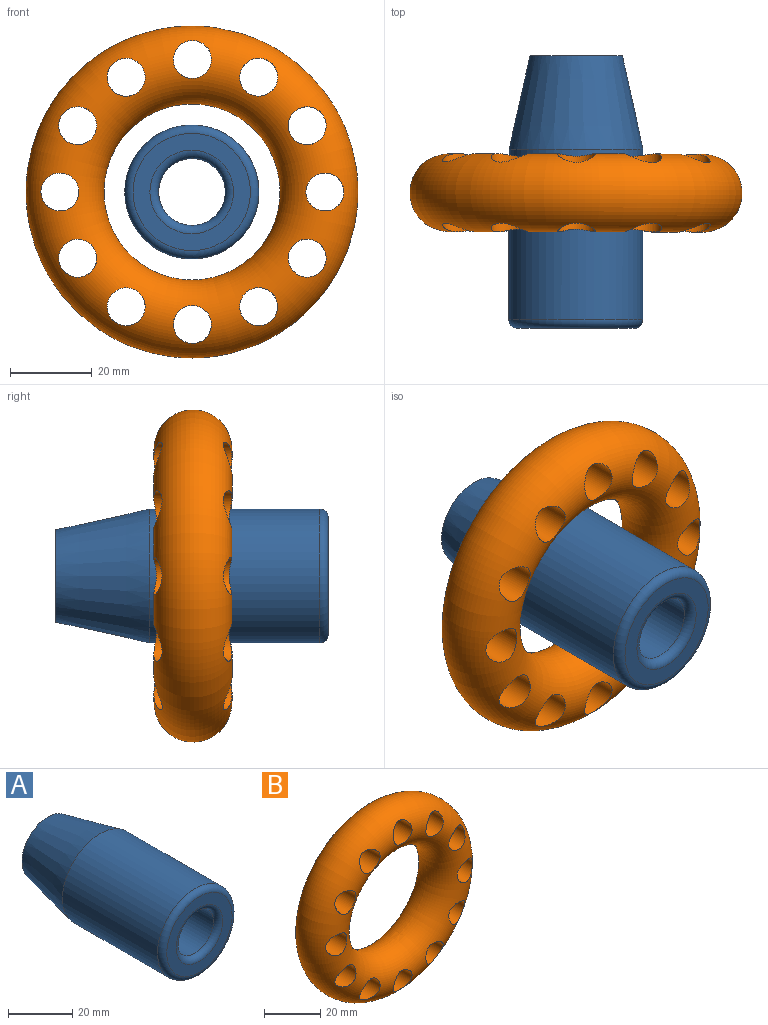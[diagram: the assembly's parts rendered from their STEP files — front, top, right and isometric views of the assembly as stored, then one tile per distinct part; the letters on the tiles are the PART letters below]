
ASSEMBLY  parts=2 mates=1
PART A: 8 faces, bbox 35.4x66.5x35.4 mm
  f0: cylinder r=16.36mm len=41.66mm, axis (0,1,0), area 4282.4mm2, adj f5,f7
  f1: plane 28.66x28.66mm, normal (0,-1,0), area 317.4mm2, adj f4,f5
  f2: plane 22.56x22.56mm, normal (0,1,0), area 38.7mm2, adj f6,f7
  f3: cylinder r=8.18mm len=61.98mm, axis (0,-1,0), area 3186mm2, adj f4,f6
  f4: torus R=10.21mm, axis (0,-1,0), area 178.9mm2, adj f1,f3
  f5: torus R=14.33mm, axis (0,-1,0), area 313.3mm2, adj f0,f1
  f6: cone r=10.72mm half-angle=45deg, axis (0,1,0), area 213.3mm2, adj f2,f3
  f7: cone r=16.36mm half-angle=12.5deg, axis (0,-1,0), area 2033.7mm2, adj f0,f2
PART B: 13 faces, bbox 87.8x19.2x87.8 mm
  f0: cylinder r=4.64mm len=19.06mm, axis (0,-1,0), area 511.6mm2, adj f11
  f1: cylinder r=4.64mm len=19.05mm, axis (0,-1,0), area 511.2mm2, adj f11
  f2: cylinder r=4.64mm len=19.04mm, axis (0,-1,0), area 511.1mm2, adj f11
  f3: cylinder r=4.64mm len=19.05mm, axis (0,-1,0), area 511.2mm2, adj f11
  f4: cylinder r=4.64mm len=19.06mm, axis (0,-1,0), area 511.6mm2, adj f11
  f5: cylinder r=4.64mm len=19.06mm, axis (0,-1,0), area 512.2mm2, adj f11
  f6: cylinder r=4.64mm len=19.06mm, axis (0,-1,0), area 512.7mm2, adj f11
  f7: cylinder r=4.64mm len=19.05mm, axis (0,-1,0), area 513.1mm2, adj f11
  f8: cylinder r=4.64mm len=19.04mm, axis (0,-1,0), area 513.2mm2, adj f11
  f9: cylinder r=4.64mm len=19.05mm, axis (0,-1,0), area 513.1mm2, adj f11
  f10: cylinder r=4.64mm len=19.06mm, axis (0,-1,0), area 512.7mm2, adj f11
  f11: torus R=31.03mm, axis (0,1,0), area 9978.3mm2, adj f0,f1,f2,f3,f4,f5,f6,f7
  f12: cylinder r=4.64mm len=19.06mm, axis (0,-1,0), area 512.3mm2, adj f11
PLACE A rot(axis=(0,1,0),90deg) t=(1,23.48,20.12)mm
PLACE B t=(1.03,-9.97,20.12)mm
MATE slider A.f0 <-> B.f11  axis (0,-1,0) through (0.87,-43.06,20.12)mm
